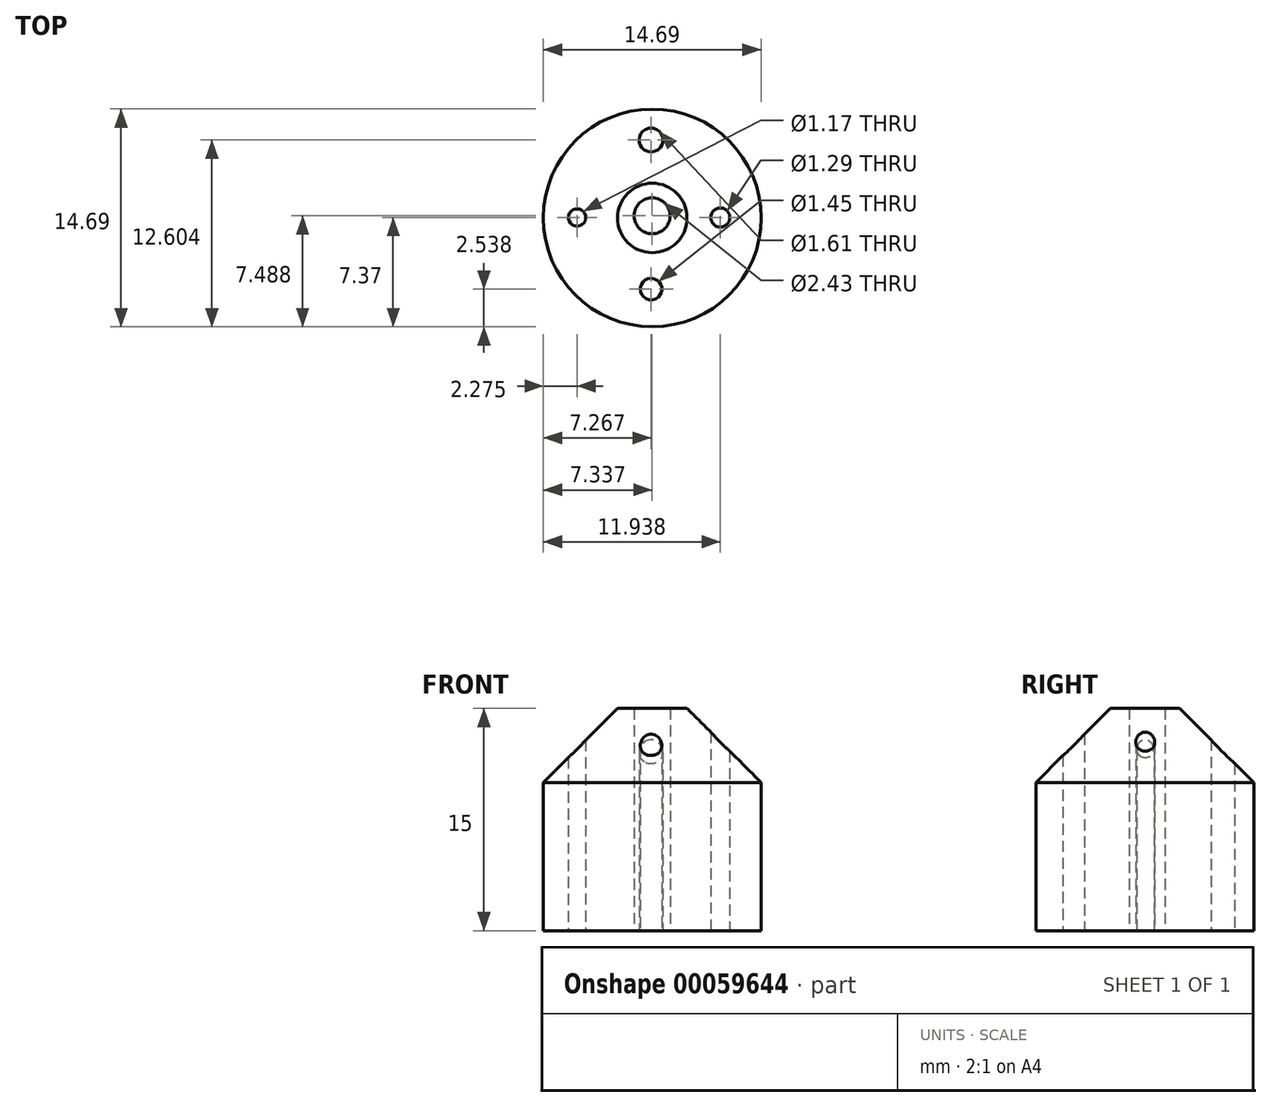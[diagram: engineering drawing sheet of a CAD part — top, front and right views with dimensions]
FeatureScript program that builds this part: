
annotation { "Feature Type Name" : "Feature", "Feature Type Description" : "" }
export const myFeature = defineFeature(function(context is Context, id is Id, definition is map)
    precondition{}
    {
        {
            var Q0;
            Q0=qCreatedBy(makeId("Top.planeOp"),FACE);
            var sketch = newSketch(context, id + "F0", { "sketchPlane" : qUnion([Q0])});
            skCircle(sketch, "E0", {"center": v(-43.48, 43.64) * mm, "radius": 7.34 * mm});
            skSolve(sketch);
        }
        {
            var Q0;
            Q0 = qSketchRegion(id + "F0", true);
            extrude(context, id + "F1", {"entities" : qUnion([Q0]), "depth" : 15 * mm});
        }
        {
            var Q0;
            Q0=makeQuery(id+"F1.opExtrude","CAP_EDGE",EDGE,{"disambiguationData":[OSD([sQuery(id+"F0.wireOp",EDGE,"E0")])],"isStart":false});
            chamfer(context, id + "F2", {"entities" : qUnion([Q0]), "width" : 5 * mm, "tangentPropagation" : true});
        }
        {
            var Q0;
            Q0=qCreatedBy(makeId("Top.planeOp"),FACE);
            var sketch = newSketch(context, id + "F3", { "sketchPlane" : qUnion([Q0])});
            skCircle(sketch, "E1", {"center": v(-43.56, 48.9) * mm, "radius": 0.8 * mm});
            skCircle(sketch, "E2", {"center": v(-43.56, 38.84) * mm, "radius": 0.72 * mm});
            skCircle(sketch, "E3", {"center": v(-38.9, 43.67) * mm, "radius": 0.64 * mm});
            skCircle(sketch, "E4", {"center": v(-48.56, 43.67) * mm, "radius": 0.59 * mm});
            skSolve(sketch);
        }
        {
            var Q0;
            Q0 = qSketchRegion(id + "F3", true);
            extrude(context, id + "F4", {"entities" : qUnion([Q0]), "operationType" : NewBodyOperationType.REMOVE, "depth" : 25 * mm});
        }
        {
            var Q0;
            Q0=qCreatedBy(makeId("Top.planeOp"),FACE);
            var sketch = newSketch(context, id + "F5", { "sketchPlane" : qUnion([Q0])});
            skCircle(sketch, "E5", {"center": v(-43.5, 43.79) * mm, "radius": 1.21 * mm});
            skSolve(sketch);
        }
        {
            var Q0;
            Q0 = qSketchRegion(id + "F5", true);
            extrude(context, id + "F6", {"entities" : qUnion([Q0]), "operationType" : NewBodyOperationType.REMOVE, "depth" : 25 * mm});
        }
    });
